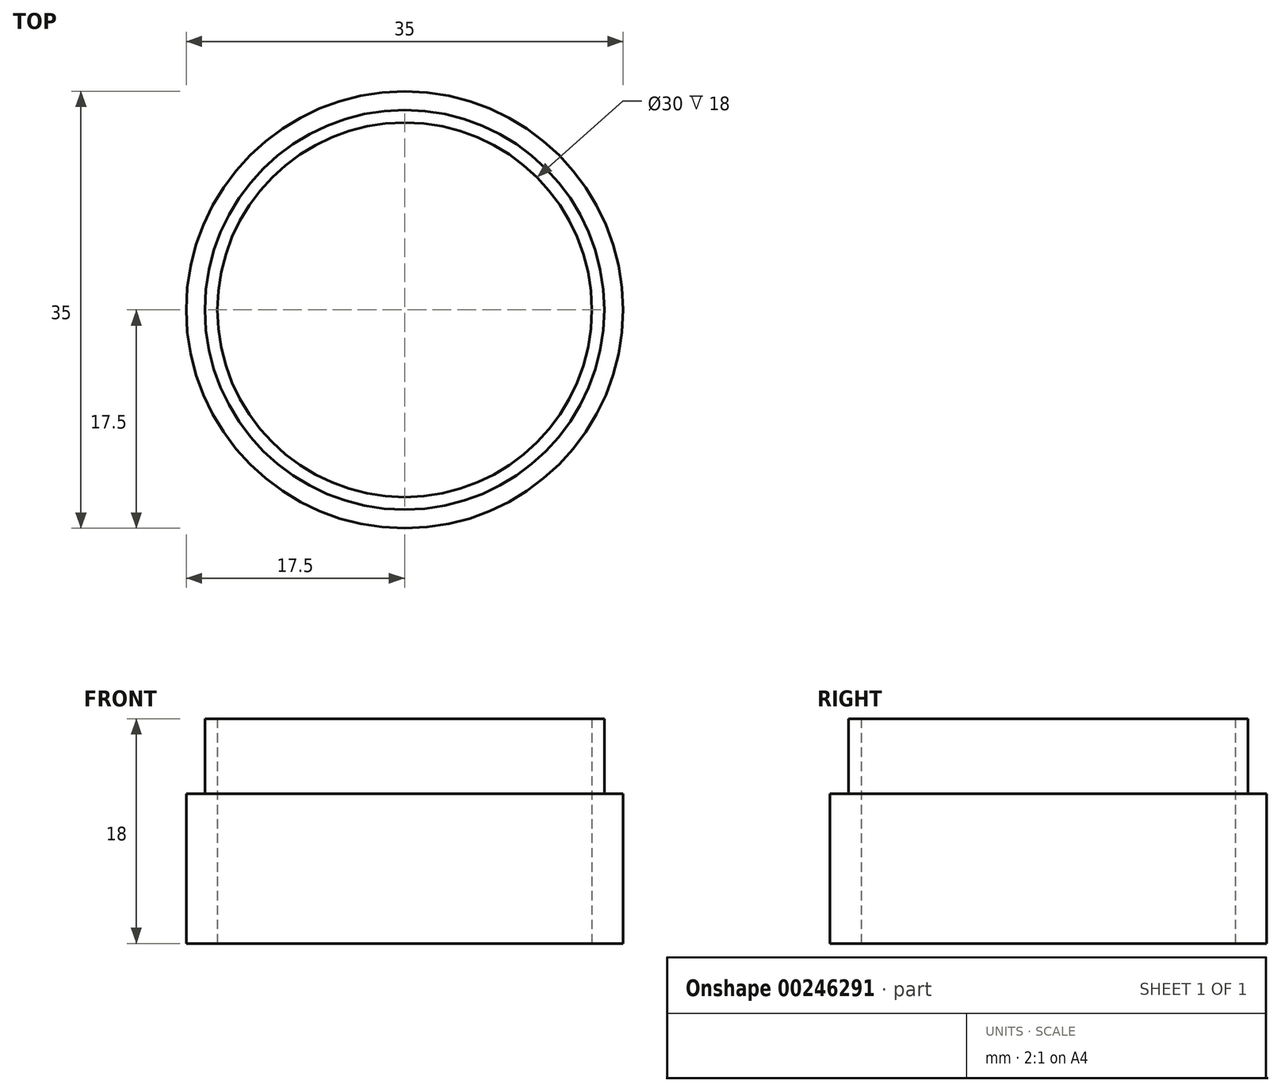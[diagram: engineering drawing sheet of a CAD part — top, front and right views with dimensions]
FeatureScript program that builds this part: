
annotation { "Feature Type Name" : "Feature", "Feature Type Description" : "" }
export const myFeature = defineFeature(function(context is Context, id is Id, definition is map)
    precondition{}
    {
        {
            var Q0;
            Q0=qCreatedBy(makeId("Top.planeOp"),FACE);
            var sketch = newSketch(context, id + "F0", { "sketchPlane" : qUnion([Q0])});
            skCircle(sketch, "E0", {"center": v(0, 0) * mm, "radius": 15 * mm});
            skCircle(sketch, "E1", {"center": v(0, 0) * mm, "radius": 16 * mm});
            skCircle(sketch, "E2", {"center": v(0, 0) * mm, "radius": 17.5 * mm});
            skSolve(sketch);
        }
        {
            var Q0;
            Q0=makeQuery(id+"F0.imprint","IMPRINT",FACE,{"disambiguationData":[TD([[makeQuery(id+"F0.imprint","IMPRINT",EDGE,{"derivedFrom":sQuery(id+"F0.wireOp",EDGE,"E0")}),-1.0]])]});
            extrude(context, id + "F1", {"entities" : qUnion([Q0]), "depth" : (12 + 6) * mm});
        }
        {
            var Q0;
            Q0=makeQuery(id+"F0.imprint","IMPRINT",FACE,{"disambiguationData":[TD([[makeQuery(id+"F0.imprint","IMPRINT",EDGE,{"derivedFrom":sQuery(id+"F0.wireOp",EDGE,"E1")}),-1.0]])]});
            extrude(context, id + "F2", {"entities" : qUnion([Q0]), "operationType" : NewBodyOperationType.ADD, "depth" : 12 * mm});
        }
    });
